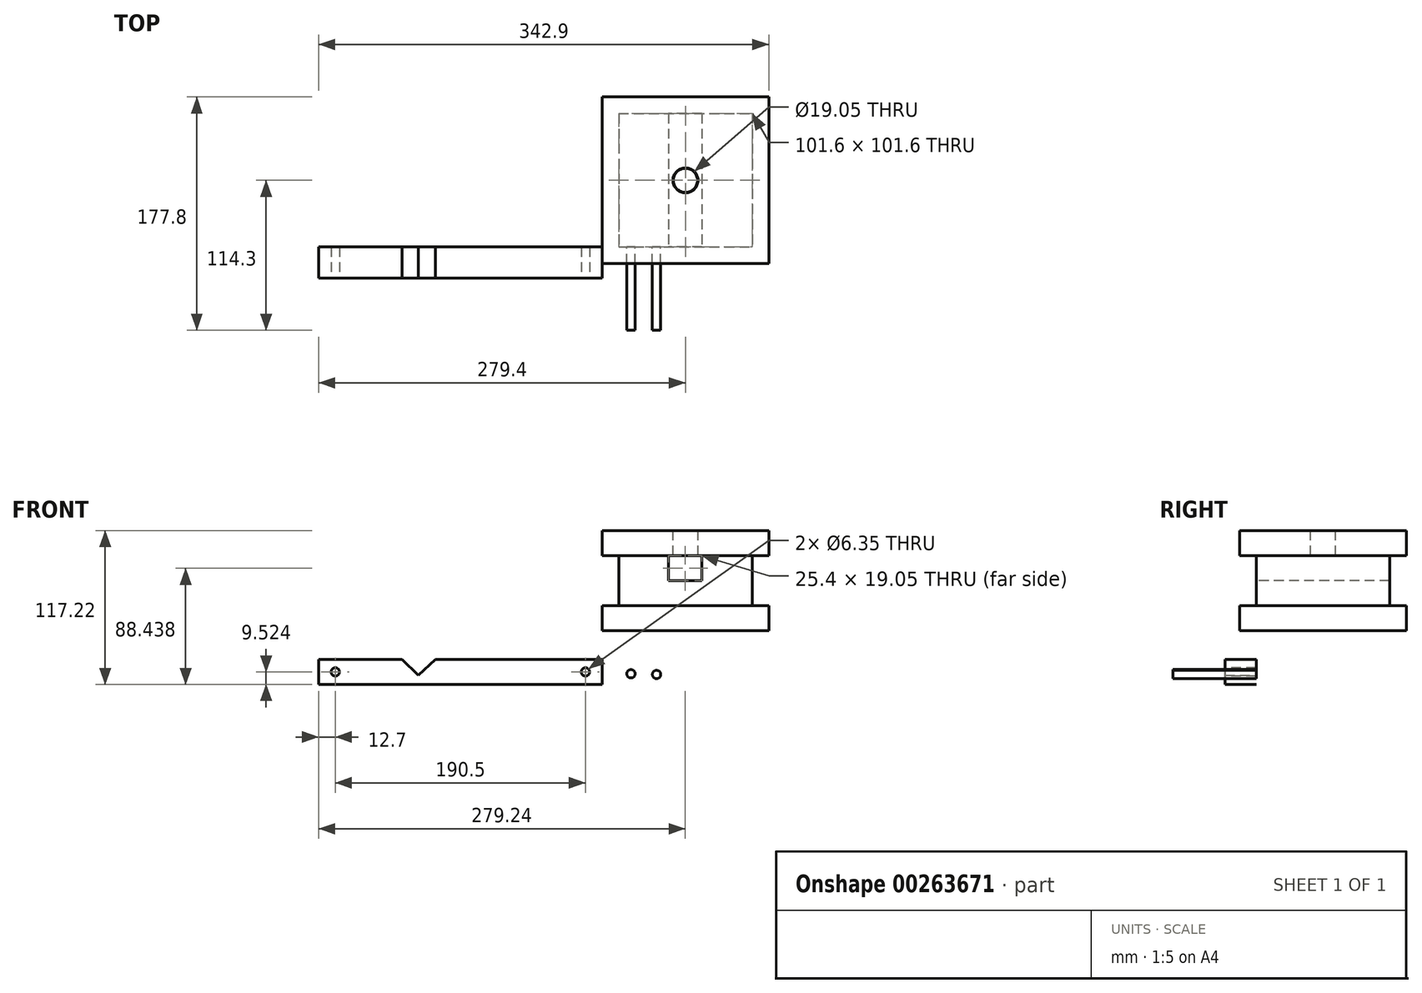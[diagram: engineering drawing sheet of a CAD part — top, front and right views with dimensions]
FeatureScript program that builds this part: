
annotation { "Feature Type Name" : "Feature", "Feature Type Description" : "" }
export const myFeature = defineFeature(function(context is Context, id is Id, definition is map)
    precondition{}
    {
        {
            var Q0;
            Q0=qCreatedBy(makeId("Front.planeOp"),FACE);
            var sketch = newSketch(context, id + "F0", { "sketchPlane" : qUnion([Q0])});
            skLineSegment(sketch, "E0", {"start": v(0, 0) * mm, "end": v(127, 0) * mm});
            skLineSegment(sketch, "E1", {"start": v(127, 0) * mm, "end": v(127, 19.05) * mm});
            skLineSegment(sketch, "E2", {"start": v(127, 19.05) * mm, "end": v(114.3, 19.05) * mm});
            skLineSegment(sketch, "E3", {"start": v(114.3, 19.05) * mm, "end": v(114.3, 57.15) * mm});
            skLineSegment(sketch, "E4", {"start": v(114.3, 57.15) * mm, "end": v(127, 57.15) * mm});
            skLineSegment(sketch, "E5", {"start": v(127, 57.15) * mm, "end": v(127, 76.2) * mm});
            skLineSegment(sketch, "E6", {"start": v(127, 76.2) * mm, "end": v(0, 76.2) * mm});
            skLineSegment(sketch, "E7", {"start": v(0, 76.2) * mm, "end": v(0, 57.15) * mm});
            skLineSegment(sketch, "E8", {"start": v(0, 57.15) * mm, "end": v(12.7, 57.15) * mm});
            skLineSegment(sketch, "E9", {"start": v(12.7, 57.15) * mm, "end": v(12.7, 19.05) * mm});
            skLineSegment(sketch, "E10", {"start": v(12.7, 19.05) * mm, "end": v(0, 19.05) * mm});
            skLineSegment(sketch, "E11", {"start": v(0, 19.05) * mm, "end": v(0, 0) * mm});
            skLineSegment(sketch, "E12", {"start": v(12.7, 57.15) * mm, "end": v(114.3, 57.15) * mm});
            skLineSegment(sketch, "E13", {"start": v(12.7, 19.05) * mm, "end": v(114.3, 19.05) * mm});
            skSolve(sketch);
        }
        {
            var Q0;
            Q0=makeQuery(id+"F0.imprint","IMPRINT",FACE,{"disambiguationData":[TD([[makeQuery(id+"F0.imprint","IMPRINT",EDGE,{"derivedFrom":sQuery(id+"F0.wireOp",EDGE,"E3")}),1.0]])]});
            extrude(context, id + "F1", {"entities" : qUnion([Q0]), "oppositeDirection" : true, "depth" : 101.6 * mm});
        }
        {
            var Q0;
            Q0=makeQuery(id+"F0.imprint","IMPRINT",FACE,{"disambiguationData":[TD([[makeQuery(id+"F0.imprint","IMPRINT",EDGE,{"derivedFrom":sQuery(id+"F0.wireOp",EDGE,"E4")}),1.0]])]});
            var Q1;
            Q1=makeQuery(id+"F0.imprint","IMPRINT",FACE,{"disambiguationData":[TD([[makeQuery(id+"F0.imprint","IMPRINT",EDGE,{"derivedFrom":sQuery(id+"F0.wireOp",EDGE,"E0")}),1.0]])]});
            extrude(context, id + "F2", {"entities" : qUnion([Q0, Q1]), "operationType" : NewBodyOperationType.ADD, "oppositeDirection" : true, "depth" : 114.3 * mm, "hasSecondDirection" : true, "secondDirectionOppositeDirection" : false, "secondDirectionDepth" : 12.7 * mm});
        }
        {
            var Q0;
            Q0=qCreatedBy(makeId("Front.planeOp"),FACE);
            var sketch = newSketch(context, id + "F3", { "sketchPlane" : qUnion([Q0])});
            skLineSegment(sketch, "E14", {"start": v(12.54, 56.94) * mm, "end": v(50.64, 56.94) * mm});
            skLineSegment(sketch, "E15", {"start": v(50.64, 56.94) * mm, "end": v(50.64, 37.9) * mm});
            skLineSegment(sketch, "E16", {"start": v(50.64, 37.9) * mm, "end": v(76.04, 37.9) * mm});
            skLineSegment(sketch, "E17", {"start": v(76.04, 37.9) * mm, "end": v(76.04, 56.94) * mm});
            skLineSegment(sketch, "E18", {"start": v(76.04, 56.94) * mm, "end": v(50.64, 56.94) * mm});
            skSolve(sketch);
        }
        {
            var Q0;
            Q0=makeQuery(id+"F3.imprint","IMPRINT",FACE,{"disambiguationData":[TD([[makeQuery(id+"F3.imprint","IMPRINT",EDGE,{"derivedFrom":sQuery(id+"F3.wireOp",EDGE,"E15")}),1.0]])]});
            extrude(context, id + "F4", {"entities" : qUnion([Q0]), "operationType" : NewBodyOperationType.REMOVE, "oppositeDirection" : true, "depth" : 127 * mm});
        }
        {
            var Q0;
            Q0=makeQuery(id+"F2.opExtrude","SWEPT_FACE",FACE,{"disambiguationData":[OSD([sQuery(id+"F0.wireOp",EDGE,"E6")])]});
            var sketch = newSketch(context, id + "F5", { "sketchPlane" : qUnion([Q0])});
            skLineSegment(sketch, "E19", {"start": v(63.5, 50.8) * mm, "end": v(127, 114.3) * mm});
            skSolve(sketch);
        }
        {
            var Q0;
            Q0=sQuery(id+"F5.wireOp",VERTEX,"E19.start");
            var Q1;
            Q1=makeQuery(id+"F1.opExtrude","SWEPT_BODY",BODY,{"disambiguationData":[OSD([sQuery(id+"F0.wireOp",EDGE,"E3"),sQuery(id+"F0.wireOp",EDGE,"E9"),sQuery(id+"F0.wireOp",EDGE,"E12"),sQuery(id+"F0.wireOp",EDGE,"E13")])]});
            hole(context, id + "F6", {"style" : HoleStyle.SIMPLE, "endStyle" : HoleEndStyle.BLIND, "holeDiameter" : 19.05 * mm, "holeDepth" : 19.05 * mm, "tappedDepth" : 12.7 * mm, "tapClearance" : 3, "locations" : qUnion([Q0]), "scope" : qUnion([Q1])});
        }
        {
            var Q0;
            Q0=qCreatedBy(makeId("Front.planeOp"),FACE);
            var sketch = newSketch(context, id + "F7", { "sketchPlane" : qUnion([Q0])});
            skLineSegment(sketch, "E20", {"start": v(0, -21.97) * mm, "end": v(0, -41.02) * mm});
            skLineSegment(sketch, "E21", {"start": v(0, -41.02) * mm, "end": v(-215.9, -41.02) * mm});
            skLineSegment(sketch, "E22", {"start": v(-215.9, -41.02) * mm, "end": v(-215.9, -21.97) * mm});
            skLineSegment(sketch, "E23", {"start": v(-215.9, -21.97) * mm, "end": v(-152.4, -21.97) * mm});
            skLineSegment(sketch, "E24", {"start": v(0, -21.97) * mm, "end": v(-127, -21.97) * mm});
            skLineSegment(sketch, "E25", {"start": v(-127, -21.97) * mm, "end": v(-139.88, -33.99) * mm});
            skLineSegment(sketch, "E26", {"start": v(-139.88, -33.99) * mm, "end": v(-152.4, -21.97) * mm});
            skSolve(sketch);
        }
        {
            var Q0;
            Q0=makeQuery(id+"F7.imprint","IMPRINT",FACE,{"disambiguationData":[TD([[makeQuery(id+"F7.imprint","IMPRINT",EDGE,{"derivedFrom":sQuery(id+"F7.wireOp",EDGE,"E20")}),-1.0]])]});
            extrude(context, id + "F8", {"entities" : qUnion([Q0]), "depth" : 23.8 * mm});
        }
        {
            var Q0;
            Q0=makeQuery(id+"F8.opExtrude","CAP_FACE",FACE,{"disambiguationData":[OSD([sQuery(id+"F7.wireOp",EDGE,"E20"),sQuery(id+"F7.wireOp",EDGE,"E21"),sQuery(id+"F7.wireOp",EDGE,"E22"),sQuery(id+"F7.wireOp",EDGE,"E23"),sQuery(id+"F7.wireOp",EDGE,"E24"),sQuery(id+"F7.wireOp",EDGE,"E25"),sQuery(id+"F7.wireOp",EDGE,"E26")])],"isStart":false});
            var sketch = newSketch(context, id + "F9", { "sketchPlane" : qUnion([Q0])});
            skLineSegment(sketch, "E27", {"start": v(-215.9, -41.02) * mm, "end": v(-215.9, -31.5) * mm});
            skLineSegment(sketch, "E28", {"start": v(-215.9, -31.5) * mm, "end": v(-203.2, -31.5) * mm});
            skLineSegment(sketch, "E29", {"start": v(0, -41.02) * mm, "end": v(0, -31.5) * mm});
            skLineSegment(sketch, "E30", {"start": v(0, -31.5) * mm, "end": v(-12.7, -31.5) * mm});
            skSolve(sketch);
        }
        {
            var Q0;
            Q0=sQuery(id+"F9.wireOp",VERTEX,"E28.end");
            var Q1;
            Q1=sQuery(id+"F9.wireOp",VERTEX,"E30.end");
            var Q2;
            Q2=makeQuery(id+"F8.opExtrude","SWEPT_BODY",BODY,{"disambiguationData":[OSD([sQuery(id+"F7.wireOp",EDGE,"E20"),sQuery(id+"F7.wireOp",EDGE,"E21"),sQuery(id+"F7.wireOp",EDGE,"E22"),sQuery(id+"F7.wireOp",EDGE,"E23"),sQuery(id+"F7.wireOp",EDGE,"E24"),sQuery(id+"F7.wireOp",EDGE,"E25"),sQuery(id+"F7.wireOp",EDGE,"E26")])]});
            hole(context, id + "F10", {"style" : HoleStyle.SIMPLE, "endStyle" : HoleEndStyle.THROUGH, "holeDiameter" : 6.35 * mm, "tappedDepth" : 12.7 * mm, "tapClearance" : 3, "locations" : qUnion([Q0, Q1]), "scope" : qUnion([Q2])});
        }
        {
            var Q0;
            Q0=qCreatedBy(makeId("Front.planeOp"),FACE);
            var sketch = newSketch(context, id + "F11", { "sketchPlane" : qUnion([Q0])});
            skCircle(sketch, "E31", {"center": v(21.97, -32.94) * mm, "radius": 3.18 * mm});
            skCircle(sketch, "E32", {"center": v(41.47, -33.46) * mm, "radius": 3.18 * mm});
            skSolve(sketch);
        }
        {
            var Q0;
            Q0=makeQuery(id+"F11.imprint","IMPRINT",FACE,{"disambiguationData":[TD([[makeQuery(id+"F11.imprint","IMPRINT",EDGE,{"derivedFrom":sQuery(id+"F11.wireOp",EDGE,"E31")}),1.0]])]});
            var Q1;
            Q1=makeQuery(id+"F11.imprint","IMPRINT",FACE,{"disambiguationData":[TD([[makeQuery(id+"F11.imprint","IMPRINT",EDGE,{"derivedFrom":sQuery(id+"F11.wireOp",EDGE,"E32")}),1.0]])]});
            extrude(context, id + "F12", {"entities" : qUnion([Q0, Q1]), "depth" : 63.5 * mm});
        }
    });
